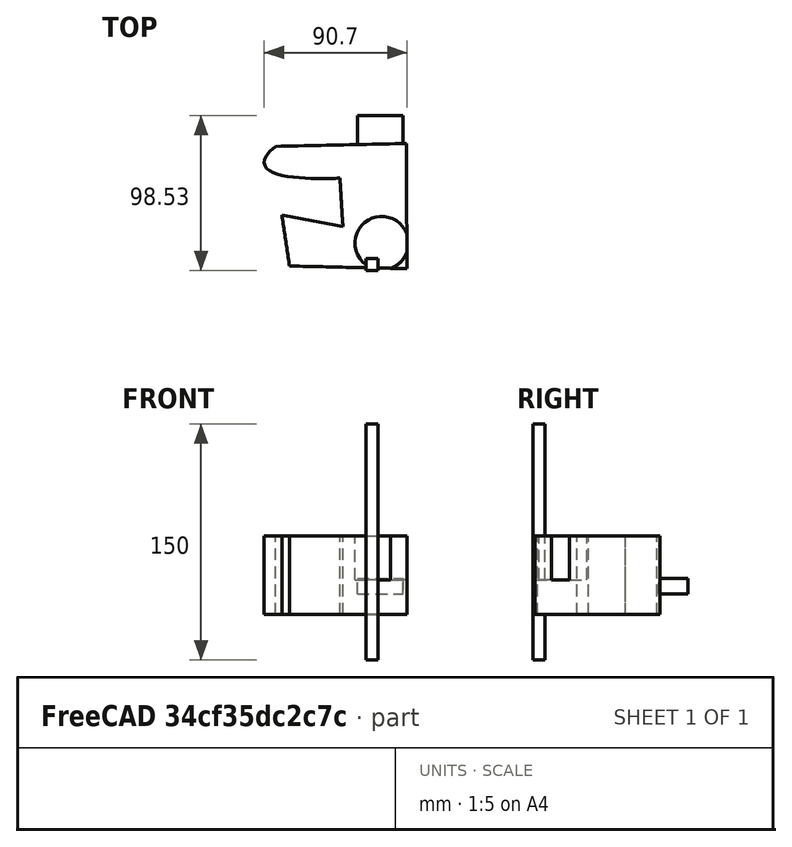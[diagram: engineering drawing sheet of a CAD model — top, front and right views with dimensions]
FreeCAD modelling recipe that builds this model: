
FCSTD DOCUMENT  (FreeCAD 0.20R29410 (Git))
Label: MangoJelly_Solutions_Tutorial_Ep6_1
License: All rights reserved
LicenseURL: http://en.wikipedia.org/wiki/All_rights_reserved
objects: Part::Feature×4, Part::Extrusion×4, Part::MultiFuse×2, Part::Cut×1
note: 11 computed .brp shape members not serialized (recipe doc carries the construction recipe); baked Part::Feature solids carry a one-line shape summary decoded from their .brp

FEATURE [Part::Feature] path111
  Placement = pos=(26.2997,-89.3854,0) rot=(0,0,1;0rad)
  shape: bbox 33.95 x 33.95 x 2e-07 mm, 1 faces, 0 solids (baked)
FEATURE [Part::Feature] rect165
  shape: bbox 29.09 x 29.09 x 2e-07 mm, 1 faces, 0 solids (baked)
FEATURE [Part::Feature] path286
  shape: bbox 100.1 x 79.49 x 2e-07 mm, 0 faces, 0 solids (baked)
FEATURE [Part::Feature] rect342
  shape: bbox 7.494 x 7.494 x 2e-07 mm, 1 faces, 0 solids (baked)
FEATURE [Part::Extrusion] Extrude
  Base = -> path286
  Dir = (0,0,1)
  DirMode = 0
  FaceMakerClass = Part::FaceMakerBullseye
  LengthFwd = 50
  LengthRev = 0
  Solid = true
  Symmetric = false
FEATURE [Part::Extrusion] Extrude001
  Base = -> rect165
  Dir = (0,0,1)
  DirMode = 0
  FaceMakerClass = Part::FaceMakerBullseye
  LengthFwd = 10
  LengthRev = 0
  Placement = pos=(0,-87,13) rot=(0,0,1;0rad)
  Solid = false
  Symmetric = false
FEATURE [Part::Extrusion] Extrude002
  Base = -> path111
  Dir = (0,0,1)
  DirMode = 0
  FaceMakerClass = Part::FaceMakerBullseye
  LengthFwd = 50
  LengthRev = 0
  Placement = pos=(97,-123,22) rot=(0,0,1;0rad)
  Solid = false
  Symmetric = false
FEATURE [Part::Cut] Cut
  Base = -> Extrude
  Tool = -> Extrude002
FEATURE [Part::MultiFuse] Fusion
  Shapes = -> [Extrude001,Cut]
FEATURE [Part::Extrusion] Extrude003
  Base = -> rect342
  Dir = (0,0,1)
  DirMode = 0
  FaceMakerClass = Part::FaceMakerBullseye
  LengthFwd = 150
  LengthRev = 0
  Placement = pos=(117,-224,-29) rot=(0,0,1;0rad)
  Solid = false
  Symmetric = false
FEATURE [Part::MultiFuse] Fusion001
  Placement = pos=(-100,130,0) rot=(0,0,1;0rad)
  Shapes = -> [Extrude003,Fusion]
